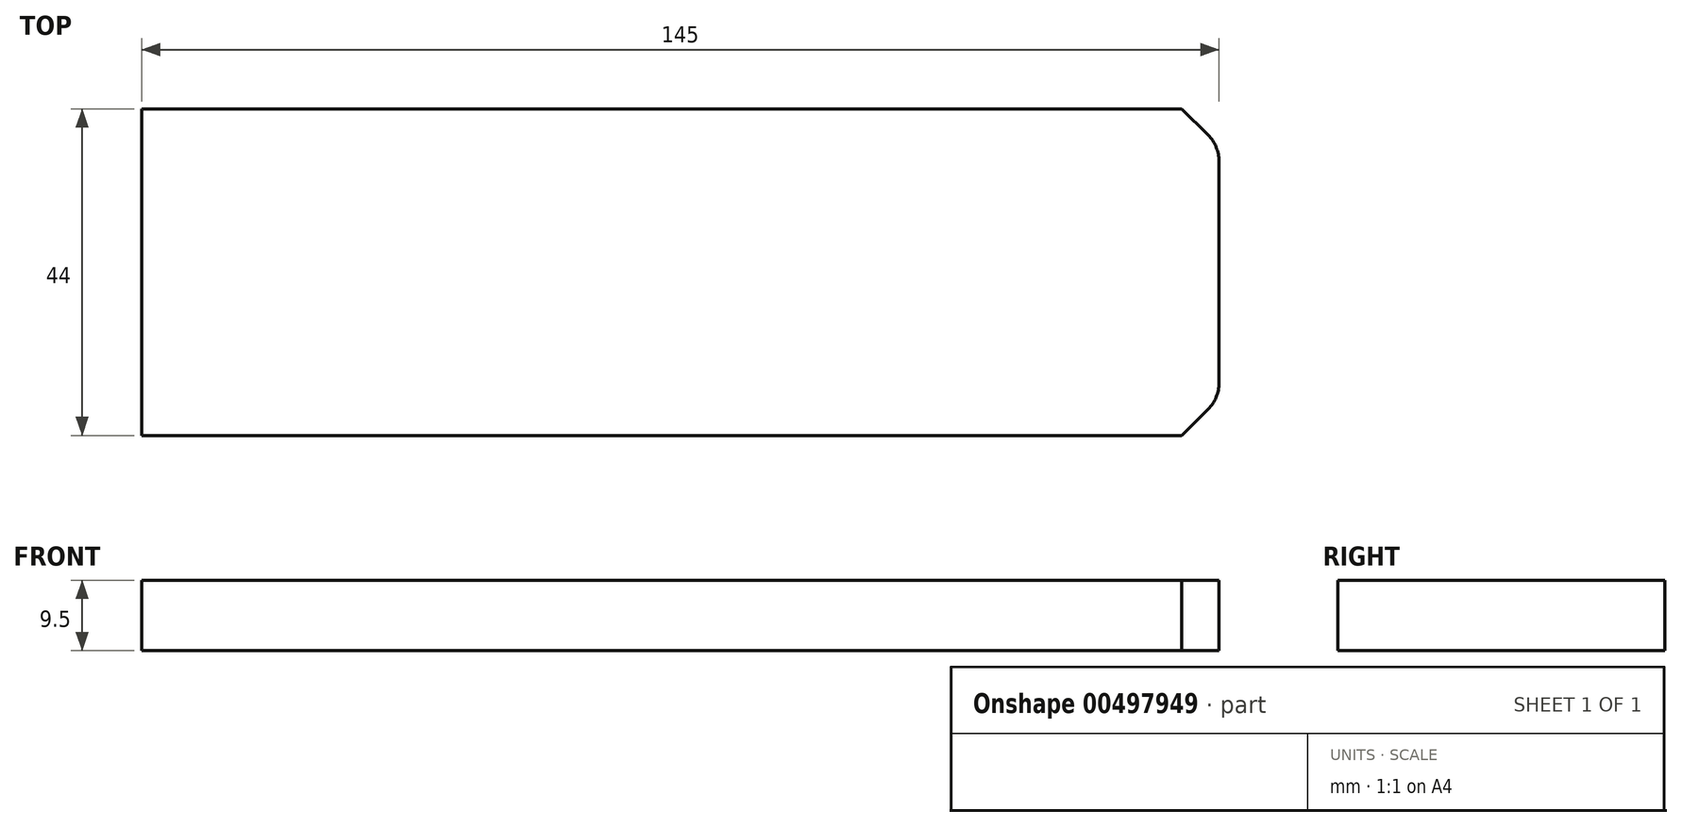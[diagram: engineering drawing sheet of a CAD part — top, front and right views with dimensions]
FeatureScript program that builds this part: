
annotation { "Feature Type Name" : "Feature", "Feature Type Description" : "" }
export const myFeature = defineFeature(function(context is Context, id is Id, definition is map)
    precondition{}
    {
        {
            var Q0;
            Q0=qCreatedBy(makeId("Front.planeOp"),FACE);
            var sketch = newSketch(context, id + "F0", { "sketchPlane" : qUnion([Q0])});
            skLineSegment(sketch, "E0.bottom", {"start": v(-72.5, 4.75) * mm, "end": v(72.5, 4.75) * mm});
            skLineSegment(sketch, "E0.top", {"start": v(-72.5, -4.75) * mm, "end": v(72.5, -4.75) * mm});
            skLineSegment(sketch, "E0.left", {"start": v(-72.5, 4.75) * mm, "end": v(-72.5, -4.75) * mm});
            skLineSegment(sketch, "E0.right", {"start": v(72.5, 4.75) * mm, "end": v(72.5, -4.75) * mm});
            skPoint(sketch, "E0.middle", {"position": v(0, 0) * mm});
            skSolve(sketch);
        }
        {
            var Q0;
            Q0 = qSketchRegion(id + "F0", true);
            extrude(context, id + "F1", {"entities" : qUnion([Q0]), "depth" : 44 * mm});
        }
        {
            var Q0;
            Q0=makeQuery(id+"F1.opExtrude","CAP_EDGE",EDGE,{"disambiguationData":[OSD([sQuery(id+"F0.wireOp",EDGE,"E0.right")])],"isStart":false});
            var Q1;
            Q1=makeQuery(id+"F1.opExtrude","CAP_EDGE",EDGE,{"disambiguationData":[OSD([sQuery(id+"F0.wireOp",EDGE,"E0.right")])],"isStart":true});
            chamfer(context, id + "F2", {"entities" : qUnion([Q0, Q1]), "width" : 5 * mm, "tangentPropagation" : true});
        }
        {
            var Q0;
            {var subQ0=sQuery(id+"F0.wireOp",EDGE,"E0.right");Q0=makeQuery(id+"F2.opChamfer","BLEND_EDGE",EDGE,{"blendedFrom":[makeQuery(id+"F1.opExtrude","CAP_EDGE",EDGE,{"disambiguationData":[OSD([subQ0])],"isStart":false}),makeQuery(id+"F1.opExtrude","SWEPT_FACE",FACE,{"disambiguationData":[OSD([subQ0])]})],"blendedInto":[makeQuery(id+"F1.opExtrude","SWEPT_FACE",FACE,{"disambiguationData":[OSD([subQ0])]})]});}
            var Q1;
            {var subQ0=sQuery(id+"F0.wireOp",EDGE,"E0.right");Q1=makeQuery(id+"F2.opChamfer","BLEND_EDGE",EDGE,{"blendedFrom":[makeQuery(id+"F1.opExtrude","CAP_EDGE",EDGE,{"disambiguationData":[OSD([subQ0])],"isStart":true}),makeQuery(id+"F1.opExtrude","SWEPT_FACE",FACE,{"disambiguationData":[OSD([subQ0])]})],"blendedInto":[makeQuery(id+"F1.opExtrude","SWEPT_FACE",FACE,{"disambiguationData":[OSD([subQ0])]})]});}
            fillet(context, id + "F3", {"entities" : qUnion([Q0, Q1]), "radius" : 5 * mm, "tangentPropagation" : true, "allowEdgeOverflow" : false});
        }
    });
